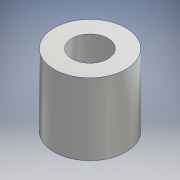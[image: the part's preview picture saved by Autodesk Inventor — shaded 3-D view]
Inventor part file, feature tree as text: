
AUTODESK INVENTOR PART (.ipt)
format: ipt  version: 2020.2 (Build 242310000, 310)  size: 131,072 bytes
history: native  units: mm
features: other x1, extrude x1, sketch x1
ambient origin geometry x8: Origin, YZ Plane, XZ Plane, XY Plane, X Axis, Y Axis, Z Axis, Center Point
bodies: Body1 (feature_tree)
feature tree (3):
  other  "ソリッド1"
  extrude  "押し出し1"  Depth=6.0mm
  sketch  "スケッチ1"
